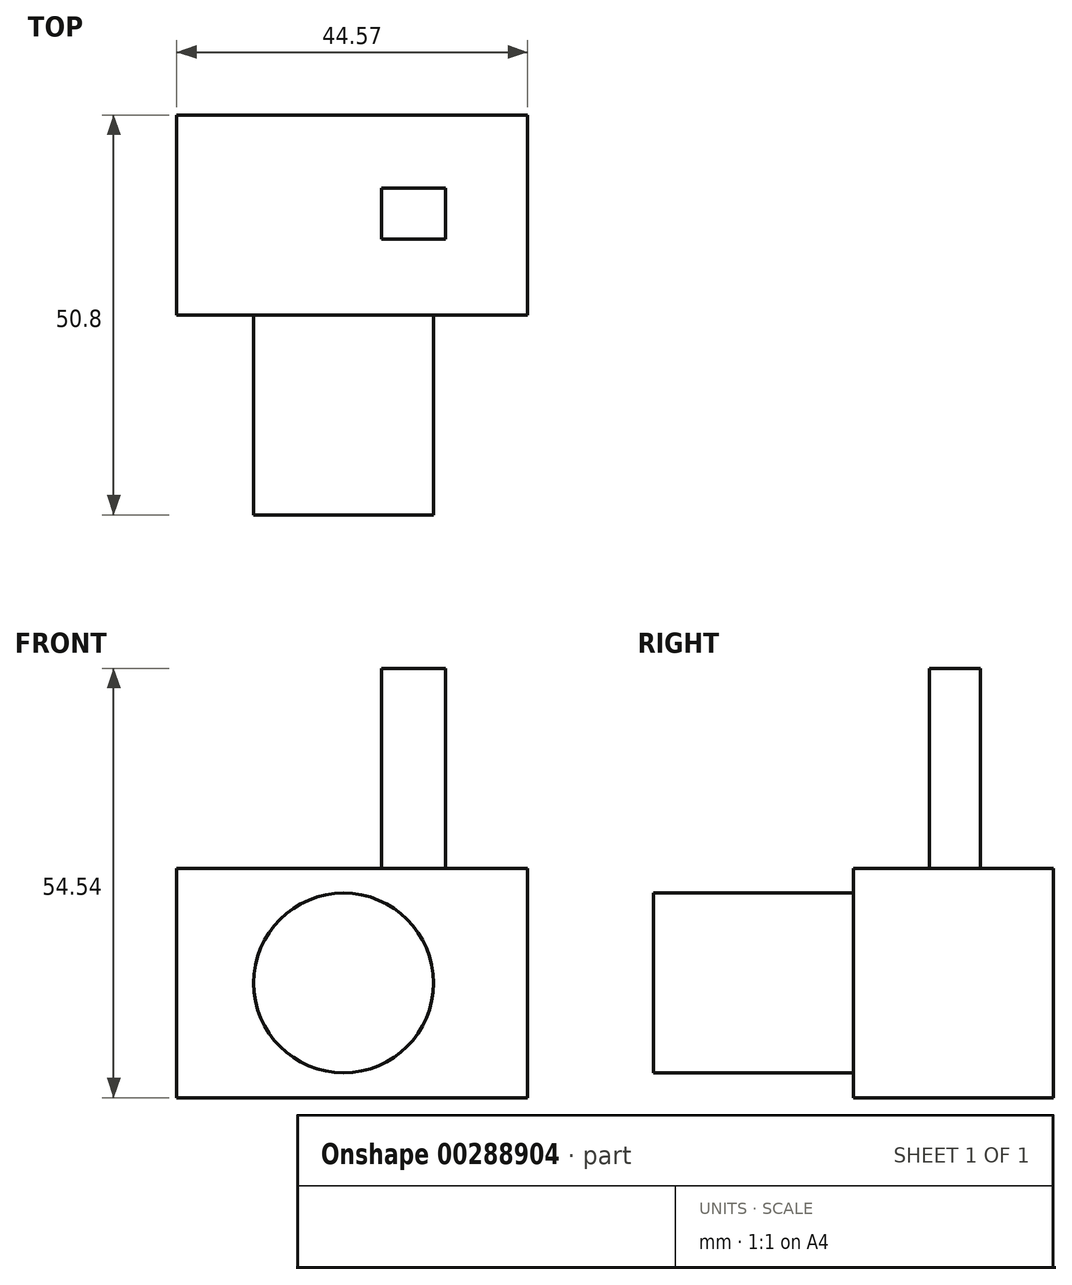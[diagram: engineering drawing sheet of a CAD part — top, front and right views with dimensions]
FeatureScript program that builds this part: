
annotation { "Feature Type Name" : "Feature", "Feature Type Description" : "" }
export const myFeature = defineFeature(function(context is Context, id is Id, definition is map)
    precondition{}
    {
        {
            var Q0;
            Q0=qCreatedBy(makeId("Front.planeOp"),FACE);
            var sketch = newSketch(context, id + "F0", { "sketchPlane" : qUnion([Q0])});
            skLineSegment(sketch, "E0.bottom", {"start": v(0, 0) * mm, "end": v(-44.57, 0) * mm});
            skLineSegment(sketch, "E0.top", {"start": v(0, 29.14) * mm, "end": v(-44.57, 29.14) * mm});
            skLineSegment(sketch, "E0.left", {"start": v(0, 0) * mm, "end": v(0, 29.14) * mm});
            skLineSegment(sketch, "E0.right", {"start": v(-44.57, 0) * mm, "end": v(-44.57, 29.14) * mm});
            skSolve(sketch);
        }
        {
            var Q0;
            Q0=makeQuery(id+"F0.imprint","IMPRINT",FACE,{"disambiguationData":[TD([[makeQuery(id+"F0.imprint","IMPRINT",EDGE,{"derivedFrom":sQuery(id+"F0.wireOp",EDGE,"E0.bottom")}),-1.0]])]});
            extrude(context, id + "F1", {"entities" : qUnion([Q0]), "depth" : 25.4 * mm});
        }
        {
            var Q0;
            Q0=makeQuery(id+"F1.opExtrude","SWEPT_FACE",FACE,{"disambiguationData":[OSD([sQuery(id+"F0.wireOp",EDGE,"E0.top")])]});
            var sketch = newSketch(context, id + "F2", { "sketchPlane" : qUnion([Q0])});
            skLineSegment(sketch, "E1.bottom", {"start": v(-18.53, -9.3) * mm, "end": v(-10.43, -9.3) * mm});
            skLineSegment(sketch, "E1.top", {"start": v(-18.53, -15.74) * mm, "end": v(-10.43, -15.74) * mm});
            skLineSegment(sketch, "E1.left", {"start": v(-18.53, -9.3) * mm, "end": v(-18.53, -15.74) * mm});
            skLineSegment(sketch, "E1.right", {"start": v(-10.43, -9.3) * mm, "end": v(-10.43, -15.74) * mm});
            skSolve(sketch);
        }
        {
            var Q0;
            Q0=makeQuery(id+"F2.imprint","IMPRINT",FACE,{"disambiguationData":[TD([[makeQuery(id+"F2.imprint","IMPRINT",EDGE,{"derivedFrom":sQuery(id+"F2.wireOp",EDGE,"E1.bottom")}),-1.0]])]});
            extrude(context, id + "F3", {"entities" : qUnion([Q0]), "operationType" : NewBodyOperationType.ADD, "depth" : 25.4 * mm});
        }
        {
            var Q0;
            Q0=makeQuery(id+"F1.opExtrude","CAP_FACE",FACE,{"disambiguationData":[OSD([sQuery(id+"F0.wireOp",EDGE,"E0.bottom"),sQuery(id+"F0.wireOp",EDGE,"E0.top"),sQuery(id+"F0.wireOp",EDGE,"E0.left"),sQuery(id+"F0.wireOp",EDGE,"E0.right")])],"isStart":false});
            var sketch = newSketch(context, id + "F4", { "sketchPlane" : qUnion([Q0])});
            skCircle(sketch, "E2", {"center": v(-23.37, 14.57) * mm, "radius": 11.41 * mm});
            skSolve(sketch);
        }
        {
            var Q0;
            Q0=makeQuery(id+"F4.imprint","IMPRINT",FACE,{"disambiguationData":[TD([[makeQuery(id+"F4.imprint","IMPRINT",EDGE,{"derivedFrom":sQuery(id+"F4.wireOp",EDGE,"E2")}),1.0]])]});
            extrude(context, id + "F5", {"entities" : qUnion([Q0]), "operationType" : NewBodyOperationType.ADD, "depth" : 25.4 * mm});
        }
    });
